# Revit family: PRD_AR_WllHngWshbsns_MEDCARESingleWashbasinBarrierFree_ANMW0046-ANMW0057
name_source: partatom
category: Plumbing Fixtures
units: mm (PartAtom-declared; Revit-internal decimal feet)

## family parameters
Cut with Voids When Loaded = Yes
Enable Cutting in Views = No
Host = Face
Maintain Annotation Orientation = No
OmniClass Number = 23.45.05.14.14
OmniClass Title = Sinks/Lavatories
Part Type = Normal
Room Calculation Point = No
Round Connector Dimension = Use Diameter
Shared = Yes

## types (12) — shared parameters
AssetType = Fixed
BarrierFree = yes
BowlPosition = Center
Category = Pr_40_20_96_96, Wall-hung washbasins
Color = alpinewhite
Colour = alpinewhite
Default Elevation = 925 mm  [stored 3.03478 ft]
DiameterNominal = 32  [stored 0.104987 ft]
DrainSize = 32 mm  [stored 0.104987 ft]
Export Type to IFC As = IfcSanitaryTerminalType
Flow = 0.0 L/s
IfcExportAs = ifcSanitaryTerminalType
IfcExportType = WASHHANDBASIN
Manufacturer = KWC Group Management AG
ManufacturerName = KWC Group Management AG
ManufacturerURL = www.kwc-professional.com
Material = mineral material
MaterialCode = Miranit
Mounting = WALLHUNG
NBSDescription = Wall hung wash basins
NBSReference = 45-35-70/369
NominalDepth = 550 mm
NominalHeight = 150 mm
NominalWidth = 850 mm  [stored 2.78871 ft]
NumberOfBowls = 1
OverallDepth = 550 mm
OverallHeight = 150 mm
OverallWidth = 850 mm  [stored 2.78871 ft]
ProductInformation = http://pim.kwc.com
RearUpstand = yes
Shape = Rectangle
SinkMaterial = PRD_AR_MineralMaterial_Alpinewhite
SiphonDiameter = DN 32
SiphonIncluded = no
Size = 850 x 150 x 550 mm (W x H x D)
Splashback = no
Status = New
TapLedge = yes
Type IFC Predefined Type = WASHHANDBASIN
TypeOfBasin = Washbasin
TypeOfMounting = wall mounting
URL = www.kwc-professional.com
Uniclass2015Code = Pr_40_20_96_96
Uniclass2015Title = Wall-hung washbasins
Uniclass2015Version = Products v1.36
Version = 1
WashHandBasinType = OTHER
WasteHolePosition = centre back
WasteSleeveIncluded = no
zero-valued in all types: MountingOffset

## per-type parameters (varying)
| type | BIMObjectName | ColourStrip | ColourStripCheck | ConnectionOffset | Description | Features | GrabRailsCheck | ModelNumber | Name | NumberOfTapHoles | Overflow | OverflowCheck | OverflowPosition | TapHoleCheck | TapHoleDiameter | TapHolePosition |
| ANMW0046 | PRD_AR_WallHungWashbasins_MEDCARESingleWashbasinBarrierFree_ANMW0046 | basalt grey | Yes | 167 mm  [stored 0.5479 ft] | MEDCARE single washbasin made of MIRANIT resin-bonded mineral material with pore-free smooth surface (temperature-resistant up to 80 °C), Alpine white colour. Roll-under, with integrated grab rails, edged with a colour strip in basalt grey. With storage areas, seamless moulded bowl, overflow and tap hole 35mm (D). Mounting on washbasin back panel. Rear surge edge, including mounting material. | Alpine white colour. Roll-under, with integrated grab rails, storage areas, seamless moulded bowl, overflow and tap hole 35 mm (D). Bowl dimensions 500 x 117 x 415 mm (W x H x D). | Yes | 2030070523 | MEDCARE Single washbasin barrier-free ANMW0046 | 1 | yes | Yes | back | Yes | 35 mm | middle |
| ANMW0047 | PRD_AR_WallHungWashbasins_MEDCARESingleWashbasinBarrierFree_ANMW0047 | no | No | 167 mm  [stored 0.5479 ft] | MEDCARE single washbasin made of MIRANIT resin-bonded mineral material with pore-free smooth surface (temperature-resistant up to 80 °C), Alpine white colour. Roll-under, with integrated grab rails, storage areas, seamless moulded bowl, overflow and tap hole 35 mm (D). Mounting on washbasin back panel. Rear surge edge, including mounting material. | Alpine white colour. Roll-under, with integrated grab rails, storage areas, seamless moulded bowl, overflow and tap hole 35 mm (D). Bowl dimensions 500 x 117 x 415 mm (W x H x D). | Yes | 2030070524 | MEDCARE Single washbasin barrier-free ANMW0047 | 1 | yes | Yes | back | Yes | 35 mm | middle |
| ANMW0048 | PRD_AR_WallHungWashbasins_MEDCARESingleWashbasinBarrierFree_ANMW0048 | basalt grey | Yes | 167 mm  [stored 0.5479 ft] | MEDCARE single washbasin made of MIRANIT resin-bonded mineral material with pore-free smooth surface (temperature-resistant up to 80 °C), Alpine white colour. Roll-under, with integrated grab rails, edged with a colour strip in basalt grey. With storage areas, seamless moulded bowl and overflow, without tap hole. Mounting on washbasin back panel. Rear surge edge, including mounting material. | Alpine white colour. Roll-under, with integrated grab rails, storage areas, seamless moulded bowl and overflow, without tap hole. Bowl dimensions 500 x 117 x 415 mm (W x H x D). | Yes | 2030072432 | MEDCARE Single washbasin barrier-free ANMW0048 |  | yes | Yes | back | No |  |  |
| ANMW0049 | PRD_AR_WallHungWashbasins_MEDCARESingleWashbasinBarrierFree_ANMW0049 | no | No | 167 mm  [stored 0.5479 ft] | MEDCARE single washbasin made of MIRANIT resin-bonded mineral material with pore-free smooth surface (temperature-resistant up to 80 °C), Alpine white colour. Roll-under, with integrated grab rails, storage areas, seamless moulded bowl and overflow, without tap hole. Mounting on washbasin back panel. Rear surge edge, including mounting material. | Alpine white colour. Roll-under, with integrated grab rails, storage areas, seamless moulded bowl and overflow, without tap hole. Bowl dimensions 500 x 117 x 415 mm (W x H x D). | Yes | 2030072433 | MEDCARE Single washbasin barrier-free ANMW0049 |  | yes | Yes | back | No |  |  |
| ANMW0050 | PRD_AR_WallHungWashbasins_MEDCARESingleWashbasinBarrierFree_ANMW0050 | basalt grey | Yes | 137 mm  [stored 0.449475 ft] | MEDCARE single washbasin made of MIRANIT resin-bonded mineral material with pore-free smooth surface (temperature-resistant up to 80 °C), Alpine white colour. Roll-under, with integrated grab rails, edged with a colour strip in basalt grey. With storage areas, seamless moulded bowl, without overflow, with tap hole 35 mm (D). Mounting on washbasin back panel. Rear surge edge, including mounting material. | Alpine white colour. Roll-under, with integrated grab rails, storage areas, seamless moulded bowl, without overflow, with tap hole 35 mm (D). Bowl dimensions 500 x 117 x 415 mm (W x H x D). | Yes | 2030072434 | MEDCARE Single washbasin barrier-free ANMW0050 | 1 | no | No |  | Yes | 35 mm | middle |
| ANMW0051 | PRD_AR_WallHungWashbasins_MEDCARESingleWashbasinBarrierFree_ANMW0051 | no | No | 137 mm  [stored 0.449475 ft] | MEDCARE single washbasin made of MIRANIT resin-bonded mineral material with pore-free smooth surface (temperature-resistant up to 80 °C), Alpine white colour. Roll-under, with integrated grab rails, storage areas, seamless moulded bowl, without overflow, with tap hole 35 mm (D). Mounting on washbasin back panel. Rear surge edge, including mounting material. | Alpine white colour. Roll-under, with integrated grab rails, storage areas, seamless moulded bowl, without overflow, with tap hole 35 mm (D). Bowl dimensions 500 x 117 x 415 mm (W x H x D). | Yes | 2030072435 | MEDCARE Single washbasin barrier-free ANMW0051 | 1 | no | No |  | Yes | 35 mm | middle |
| ANMW0052 | PRD_AR_WallHungWashbasins_MEDCARESingleWashbasinBarrierFree_ANMW0052 | basalt grey | Yes | 137 mm  [stored 0.449475 ft] | MEDCARE single washbasin made of MIRANIT resin-bonded mineral material with pore-free smooth surface (temperature-resistant up to 80 °C), Alpine white colour. Roll-under, with integrated grab rails, edged with a colour strip in basalt grey. With storage areas, seamless moulded bowl, without overflow, without tap hole. Mounting on washbasin back panel. Rear surge edge, including mounting material. | Alpine white colour. Roll-under, with integrated grab rails, storage areas, seamless moulded bowl, without overflow, without tap hole. Bowl dimensions 500 x 117 x 415 mm (W x H x D). | Yes | 2030072436 | MEDCARE Single washbasin barrier-free ANMW0052 |  | no | No |  | No |  |  |
| ANMW0053 | PRD_AR_WallHungWashbasins_MEDCARESingleWashbasinBarrierFree_ANMW0053 | no | No | 137 mm  [stored 0.449475 ft] | MEDCARE single washbasin made of MIRANIT resin-bonded mineral material with pore-free smooth surface (temperature-resistant up to 80 °C), Alpine white colour. Roll-under, with integrated grab rails, storage areas, seamless moulded bowl, without overflow, without tap hole. Mounting on washbasin back panel. Rear surge edge, including mounting material. | Alpine white colour. Roll-under, with integrated grab rails, storage areas, seamless moulded bowl, without overflow, without tap hole. Bowl dimensions 500 x 117 x 415 mm (W x H x D). | Yes | 2030072437 | MEDCARE Single washbasin barrier-free ANMW0053 |  | no | No |  | No |  |  |
| ANMW0054 | PRD_AR_WallHungWashbasins_MEDCARESingleWashbasinBarrierFree_ANMW0054 | no | No | 167 mm  [stored 0.5479 ft] | MEDCARE single washbasin made of MIRANIT resin-bonded mineral material with pore-free smooth surface (temperature-resistant up to 80 °C), Alpine white colour. Roll-under, with storage areas, seamless moulded bowl, overflow and tap hole 35 mm (D). Mounting on washbasin back panel. Rear surge edge, including mounting material. | Alpine white colour. Roll-under, with storage areas, seamless moulded bowl, overflow and tap hole 35 mm (D). Bowl dimensions 500 x 117 x 415 mm (W x H x D). | No | 2030072438 | MEDCARE Single washbasin barrier-free ANMW0054 | 1 | yes | Yes | back | Yes | 35 mm | middle |
| ANMW0055 | PRD_AR_WallHungWashbasins_MEDCARESingleWashbasinBarrierFree_ANMW0055 | no | No | 167 mm  [stored 0.5479 ft] | MEDCARE single washbasin made of MIRANIT resin-bonded mineral material with pore-free smooth surface (temperature-resistant up to 80 °C), Alpine white colour. Roll-under, with storage areas, seamless moulded bowl and overflow, without tap hole. Mounting on washbasin back panel. Rear surge edge, including mounting material. | Alpine white colour. Roll-under, with storage areas, seamless moulded bowl and overflow, without tap hole. Bowl dimensions 500 x 117 x 415 mm (W x H x D). | No | 2030072439 | MEDCARE Single washbasin barrier-free ANMW0055 |  | yes | Yes | back | No |  |  |
| ANMW0056 | PRD_AR_WallHungWashbasins_MEDCARESingleWashbasinBarrierFree_ANMW0056 | no | No | 137 mm  [stored 0.449475 ft] | MEDCARE single washbasin made of MIRANIT resin-bonded mineral material with pore-free smooth surface (temperature-resistant up to 80 °C), Alpine white colour. Roll-under, with storage areas, seamless moulded bowl, without overflow, with tap hole 35mm (D). Mounting on washbasin back panel. Rear surge edge, including mounting material. | Alpine white colour. Roll-under, with storage areas, seamless moulded bowl, without overflow, with tap hole 35 mm (D). Bowl dimensions 500 x 117 x 415 mm (W x H x D). | No | 2030072440 | MEDCARE Single washbasin barrier-free ANMW0056 | 1 | no | No |  | Yes | 35 mm | middle |
| ANMW0057 | PRD_AR_WallHungWashbasins_MEDCARESingleWashbasinBarrierFree_ANMW0057 | no | No | 137 mm  [stored 0.449475 ft] | MEDCARE single washbasin made of MIRANIT resin-bonded mineral material with pore-free smooth surface (temperature-resistant up to 80 °C), Alpine white colour. Roll-under, with storage areas and seamless moulded bowl, without overflow, without tap hole. Mounting on washbasin back panel. Rear surge edge, including mounting material. | Alpine white colour. Roll-under, with storage areas and seamless moulded bowl, without overflow, without tap hole. Bowl dimensions 500 x 117 x 415 mm (W x H x D). | No | 2030072441 | MEDCARE Single washbasin barrier-free ANMW0057 |  | no | No |  | No |  |  |

note: column(s) folded — value = type name in every type: Model, ModelReference

note: [stored X ft] marks values corroborated as IEEE doubles in the binary element streams (Revit-internal decimal feet)

## geometry (parser evidence)
native form markers: Sweep x4
no freeform markers — native parametric forms only
